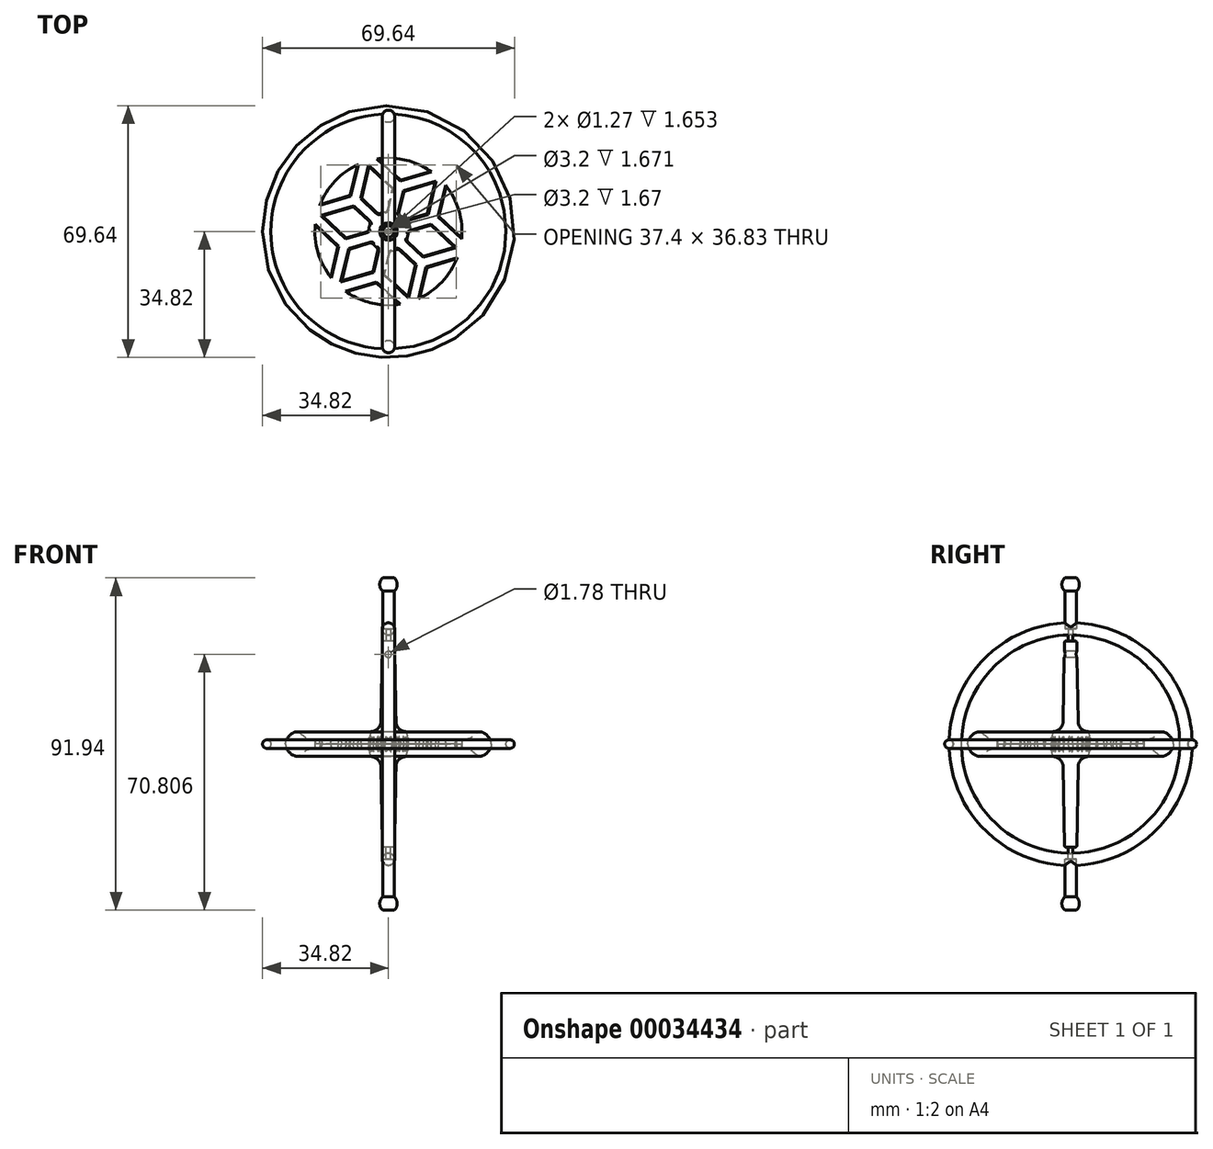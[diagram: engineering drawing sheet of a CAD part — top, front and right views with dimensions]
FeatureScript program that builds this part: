
annotation { "Feature Type Name" : "Feature", "Feature Type Description" : "" }
export const myFeature = defineFeature(function(context is Context, id is Id, definition is map)
    precondition{}
    {
        {
            var Q0;
            Q0=qCreatedBy(makeId("Top.planeOp"),FACE);
            var sketch = newSketch(context, id + "F0", { "sketchPlane" : qUnion([Q0])});
            skCircle(sketch, "E0", {"center": v(0, 0) * mm, "radius": 5.46 * mm});
            skSolve(sketch);
        }
        {
            var Q0;
            Q0 = qSketchRegion(id + "F0", true);
            extrude(context, id + "F1", {"entities" : qUnion([Q0]), "depth" : 3.43 * mm, "hasDraft" : true, "draftAngle" : 8 * degree, "draftPullDirection" : true});
        }
        {
            var Q0;
            Q0=qCreatedBy(makeId("Front.planeOp"),FACE);
            var sketch = newSketch(context, id + "F2", { "sketchPlane" : qUnion([Q0])});
            skLineSegment(sketch, "E1.0", {"start": v(-4.98, 3.43) * mm, "end": v(4.98, 3.43) * mm, "construction": true});
            skLineSegment(sketch, "E2", {"start": v(0, 3.43) * mm, "end": v(0, 14.25) * mm, "construction": true});
            skPoint(sketch, "E2.endSnap0", {"position": v(0, 3.43) * mm});
            skArc(sketch, "E3", {"start": v(2.07, 6.34) * mm, "mid": v(2.92, 4.28) * mm, "end": v(4.98, 3.43) * mm});
            skLineSegment(sketch, "E4", {"start": v(2.07, 6.34) * mm, "end": v(2.07, 12.69) * mm, "construction": true});
            skLineSegment(sketch, "E5", {"start": v(2.07, 6.34) * mm, "end": v(0, 6.34) * mm});
            skLineSegment(sketch, "E6", {"start": v(0, 6.34) * mm, "end": v(0, 3.43) * mm});
            skLineSegment(sketch, "E7", {"start": v(0, 3.43) * mm, "end": v(4.98, 3.43) * mm});
            skSolve(sketch);
        }
        {
            var Q0;
            Q0=makeQuery(id+"F2.imprint","IMPRINT",FACE,{"disambiguationData":[TD([[makeQuery(id+"F2.imprint","IMPRINT",EDGE,{"derivedFrom":sQuery(id+"F2.wireOp",EDGE,"E3")}),-1.0]])]});
            var Q1;
            Q1=sQuery(id+"F2.wireOp",EDGE,"E2");
            revolve(context, id + "F3", {"operationType" : NewBodyOperationType.ADD, "entities" : qUnion([Q0]), "axis" : qUnion([Q1]), "revolveType" : RevolveType.FULL});
        }
        {
            var Q0;
            Q0=makeQuery(id+"F3.opRevolve","SWEPT_FACE",FACE,{"disambiguationData":[OSD([sQuery(id+"F2.wireOp",EDGE,"E5")])]});
            var sketch = newSketch(context, id + "F4", { "sketchPlane" : qUnion([Q0])});
            skCircle(sketch, "E8.1", {"center": v(0, 0) * mm, "radius": 2.07 * mm});
            skSolve(sketch);
        }
        {
            var Q0;
            Q0 = qSketchRegion(id + "F4", true);
            extrude(context, id + "F5", {"entities" : qUnion([Q0]), "operationType" : NewBodyOperationType.ADD, "depth" : 22.17 * mm, "hasDraft" : true, "draftAngle" : 1 * degree, "draftPullDirection" : true});
        }
        {
            var Q0;
            Q0=qCreatedBy(makeId("Top.planeOp"),FACE);
            var sketch = newSketch(context, id + "F6", { "sketchPlane" : qUnion([Q0])});
            skLineSegment(sketch, "E9", {"start": v(0, 0) * mm, "end": v(-9.24, 8.72) * mm});
            skLineSegment(sketch, "E10", {"start": v(0, 0) * mm, "end": v(-12.17, -3.64) * mm});
            skLineSegment(sketch, "E11", {"start": v(-9.24, 8.72) * mm, "end": v(-21.4, 5.08) * mm});
            skLineSegment(sketch, "E12", {"start": v(-21.4, 5.08) * mm, "end": v(-12.17, -3.64) * mm});
            skLineSegment(sketch, "E13", {"start": v(-21.4, 5.08) * mm, "end": v(0, 0) * mm, "construction": true});
            skLineSegment(sketch, "E14", {"start": v(-12.17, -3.64) * mm, "end": v(-15.1, -16) * mm});
            skLineSegment(sketch, "E15.0", {"start": v(-3.14, 0.74) * mm, "end": v(-11.74, -1.83) * mm});
            skLineSegment(sketch, "E15.1", {"start": v(-3.14, 0.74) * mm, "end": v(-9.67, 6.9) * mm});
            skLineSegment(sketch, "E15.2", {"start": v(-9.67, 6.9) * mm, "end": v(-18.26, 4.33) * mm});
            skLineSegment(sketch, "E15.3", {"start": v(-18.26, 4.33) * mm, "end": v(-11.74, -1.83) * mm});
            skLineSegment(sketch, "E16.0", {"start": v(3.14, -0.74) * mm, "end": v(-12.6, -5.45) * mm});
            skLineSegment(sketch, "E16.1", {"start": v(3.14, -0.74) * mm, "end": v(-8.8, 10.53) * mm});
            skLineSegment(sketch, "E16.2", {"start": v(-8.8, 10.53) * mm, "end": v(-24.54, 5.82) * mm});
            skLineSegment(sketch, "E16.3", {"start": v(-24.54, 5.82) * mm, "end": v(-12.6, -5.45) * mm});
            skLineSegment(sketch, "E17.0", {"start": v(-13.74, -3.27) * mm, "end": v(-16.67, -15.62) * mm});
            skLineSegment(sketch, "E18.0", {"start": v(-10.6, -4.01) * mm, "end": v(-13.53, -16.37) * mm});
            skLineSegment(sketch, "E19", {"start": v(-13.53, -16.37) * mm, "end": v(-15.1, -16) * mm});
            skLineSegment(sketch, "E20", {"start": v(-16.67, -15.62) * mm, "end": v(-15.1, -16) * mm});
            skSolve(sketch);
        }
        {
            var Q0;
            Q0=makeQuery(id+"F6.imprint","IMPRINT",FACE,{"disambiguationData":[TD([[makeQuery(id+"F6.imprint","IMPRINT",EDGE,{"derivedFrom":sQuery(id+"F6.wireOp",EDGE,"E9")}),1.0]])]});
            var Q1;
            Q1=makeQuery(id+"F6.imprint","IMPRINT",FACE,{"disambiguationData":[TD([[makeQuery(id+"F6.imprint","IMPRINT",EDGE,{"derivedFrom":sQuery(id+"F6.wireOp",EDGE,"E9")}),-1.0]])]});
            var Q2;
            {var subQ0=sQuery(id+"F6.wireOp",EDGE,"E19");Q2=makeQuery(id+"F6.imprint","IMPRINT",FACE,{"disambiguationData":[TD([[makeQuery(id+"F6.imprint","IMPRINT",EDGE,{"derivedFrom":subQ0}),-1.0]])]});}
            var Q3;
            {var subQ0=sQuery(id+"F6.wireOp",EDGE,"E20");Q3=makeQuery(id+"F6.imprint","IMPRINT",FACE,{"disambiguationData":[TD([[makeQuery(id+"F6.imprint","IMPRINT",EDGE,{"derivedFrom":subQ0}),1.0]])]});}
            extrude(context, id + "F7", {"entities" : qUnion([Q0, Q1, Q2, Q3]), "depth" : 1.27 * mm, "hasDraft" : true, "draftAngle" : 10 * degree, "draftPullDirection" : true});
        }
        {
            var Q0;
            Q0=makeQuery(id+"F7.opExtrude","SWEPT_BODY",BODY,{"disambiguationData":[OSD([sQuery(id+"F6.wireOp",EDGE,"E15.0"),sQuery(id+"F6.wireOp",EDGE,"E15.1"),sQuery(id+"F6.wireOp",EDGE,"E15.2"),sQuery(id+"F6.wireOp",EDGE,"E15.3"),sQuery(id+"F6.wireOp",EDGE,"E16.0"),sQuery(id+"F6.wireOp",EDGE,"E16.1"),sQuery(id+"F6.wireOp",EDGE,"E16.2"),sQuery(id+"F6.wireOp",EDGE,"E16.3"),sQuery(id+"F6.wireOp",EDGE,"E17.0"),sQuery(id+"F6.wireOp",EDGE,"E18.0"),sQuery(id+"F6.wireOp",EDGE,"E19"),sQuery(id+"F6.wireOp",EDGE,"E20")])]});
            var Q1;
            Q1=sQuery(id+"F2.wireOp",EDGE,"E2");
            circularPattern(context, id + "F8", {"operationType" : NewBodyOperationType.ADD, "entities" : qUnion([Q0]), "axis" : qUnion([Q1]), "angle" : 60 * degree, "instanceCount" : 6});
        }
        {
            var Q0;
            Q0=qCreatedBy(makeId("Top.planeOp"),FACE);
            var sketch = newSketch(context, id + "F9", { "sketchPlane" : qUnion([Q0])});
            skCircle(sketch, "E21", {"center": v(0, 0) * mm, "radius": 20.32 * mm});
            skCircle(sketch, "E22", {"center": v(0, 0) * mm, "radius": 25.4 * mm});
            skSolve(sketch);
        }
        {
            var Q0;
            Q0=makeQuery(id+"F9.imprint","IMPRINT",FACE,{"disambiguationData":[TD([[makeQuery(id+"F9.imprint","IMPRINT",EDGE,{"derivedFrom":sQuery(id+"F9.wireOp",EDGE,"E21")}),-1.0]])]});
            extrude(context, id + "F10", {"entities" : qUnion([Q0]), "operationType" : NewBodyOperationType.ADD, "depth" : 1.27 * mm});
        }
        {
            var Q0;
            Q0=qCreatedBy(makeId("Front.planeOp"),FACE);
            var sketch = newSketch(context, id + "F11", { "sketchPlane" : qUnion([Q0])});
            skLineSegment(sketch, "E23.0", {"start": v(-25.4, 0) * mm, "end": v(25.4, 0) * mm, "construction": true});
            skLineSegment(sketch, "E24", {"start": v(25.4, 0) * mm, "end": v(28.45, 0) * mm, "construction": true});
            skLineSegment(sketch, "E25.0", {"start": v(-25.4, 1.27) * mm, "end": v(25.4, 1.27) * mm, "construction": true});
            skLineSegment(sketch, "E26", {"start": v(28.45, 0) * mm, "end": v(28.45, 3.38) * mm, "construction": true});
            skLineSegment(sketch, "E27.0", {"start": v(15.77, 1.27) * mm, "end": v(20.32, 1.27) * mm, "construction": true});
            skLineSegment(sketch, "E28", {"start": v(20.32, 1.27) * mm, "end": v(20.32, 3.38) * mm, "construction": true});
            skLineSegment(sketch, "E29", {"start": v(25.32, 0) * mm, "end": v(25.32, 3.38) * mm, "construction": true});
            skLineSegment(sketch, "E30", {"start": v(28.45, 3.38) * mm, "end": v(20.32, 3.38) * mm, "construction": true});
            skFitSpline(sketch, "E31", {"points": [v(20.32, 1.27) * mm, v(25.32, 3.38) * mm, v(28.45, 0) * mm], "startDerivative": vector(18.65, 0) * mm, "endDerivative": vector(0, -10.57) * mm});
            skLineSegment(sketch, "E32", {"start": v(20.32, 1.27) * mm, "end": v(25.4, 1.27) * mm});
            skLineSegment(sketch, "E33", {"start": v(25.4, 1.27) * mm, "end": v(25.4, 0) * mm});
            skLineSegment(sketch, "E34", {"start": v(25.4, 0) * mm, "end": v(28.45, 0) * mm});
            skSolve(sketch);
        }
        {
            var Q0;
            Q0 = qSketchRegion(id + "F11", true);
            var Q1;
            Q1=sQuery(id+"F2.wireOp",EDGE,"E2");
            revolve(context, id + "F12", {"operationType" : NewBodyOperationType.ADD, "entities" : qUnion([Q0]), "axis" : qUnion([Q1]), "revolveType" : RevolveType.FULL});
        }
        {
            var Q0;
            Q0=makeQuery(id+"F5.opExtrude","CAP_EDGE",EDGE,{"disambiguationData":[OSD([sQuery(id+"F4.wireOp",EDGE,"E8.1")])],"isStart":false});
            fillet(context, id + "F13", {"entities" : qUnion([Q0]), "radius" : 0.38 * mm, "tangentPropagation" : true, "allowEdgeOverflow" : false});
        }
        {
            var Q0;
            Q0=makeQuery(id+"F5.opExtrude","CAP_FACE",FACE,{"disambiguationData":[OSD([sQuery(id+"F4.wireOp",EDGE,"E8.1")])],"isStart":false});
            var sketch = newSketch(context, id + "F14", { "sketchPlane" : qUnion([Q0])});
            skCircle(sketch, "E35", {"center": v(0, 0) * mm, "radius": 0.64 * mm});
            skSolve(sketch);
        }
        {
            var Q0;
            Q0 = qSketchRegion(id + "F14", true);
            extrude(context, id + "F15", {"entities" : qUnion([Q0]), "operationType" : NewBodyOperationType.ADD, "depth" : 3.3 * mm});
        }
        {
            var Q0;
            {var subQ0=makeQuery(id+"F7.opExtrude","CAP_FACE",FACE,{"disambiguationData":[OSD([sQuery(id+"F6.wireOp",EDGE,"E15.0"),sQuery(id+"F6.wireOp",EDGE,"E15.1"),sQuery(id+"F6.wireOp",EDGE,"E15.2"),sQuery(id+"F6.wireOp",EDGE,"E15.3"),sQuery(id+"F6.wireOp",EDGE,"E16.0"),sQuery(id+"F6.wireOp",EDGE,"E16.1"),sQuery(id+"F6.wireOp",EDGE,"E16.2"),sQuery(id+"F6.wireOp",EDGE,"E16.3"),sQuery(id+"F6.wireOp",EDGE,"E17.0"),sQuery(id+"F6.wireOp",EDGE,"E18.0"),sQuery(id+"F6.wireOp",EDGE,"E19"),sQuery(id+"F6.wireOp",EDGE,"E20")])],"isStart":false});Q0=makeQuery(id+"F8.boolean.opBoolean","INTERSECT",EDGE,{"disambiguationData":[OD(4.0)],"derivedFrom":[makeQuery(id+"F1.opExtrude","SWEPT_FACE",FACE,{"disambiguationData":[OSD([sQuery(id+"F0.wireOp",EDGE,"E0")])]}),subQ0,makeQuery(id+"F8.opPattern","COPY",FACE,{"derivedFrom":subQ0,"instanceName":"1"}),makeQuery(id+"F8.opPattern","COPY",FACE,{"derivedFrom":subQ0,"instanceName":"2"}),makeQuery(id+"F8.opPattern","COPY",FACE,{"derivedFrom":subQ0,"instanceName":"3"}),makeQuery(id+"F8.opPattern","COPY",FACE,{"derivedFrom":subQ0,"instanceName":"4"}),makeQuery(id+"F8.opPattern","COPY",FACE,{"derivedFrom":subQ0,"instanceName":"5"})]});}
            var Q1;
            {var subQ0=makeQuery(id+"F7.opExtrude","CAP_FACE",FACE,{"disambiguationData":[OSD([sQuery(id+"F6.wireOp",EDGE,"E15.0"),sQuery(id+"F6.wireOp",EDGE,"E15.1"),sQuery(id+"F6.wireOp",EDGE,"E15.2"),sQuery(id+"F6.wireOp",EDGE,"E15.3"),sQuery(id+"F6.wireOp",EDGE,"E16.0"),sQuery(id+"F6.wireOp",EDGE,"E16.1"),sQuery(id+"F6.wireOp",EDGE,"E16.2"),sQuery(id+"F6.wireOp",EDGE,"E16.3"),sQuery(id+"F6.wireOp",EDGE,"E17.0"),sQuery(id+"F6.wireOp",EDGE,"E18.0"),sQuery(id+"F6.wireOp",EDGE,"E19"),sQuery(id+"F6.wireOp",EDGE,"E20")])],"isStart":false});Q1=makeQuery(id+"F8.boolean.opBoolean","INTERSECT",EDGE,{"disambiguationData":[OD(5.0)],"derivedFrom":[makeQuery(id+"F1.opExtrude","SWEPT_FACE",FACE,{"disambiguationData":[OSD([sQuery(id+"F0.wireOp",EDGE,"E0")])]}),subQ0,makeQuery(id+"F8.opPattern","COPY",FACE,{"derivedFrom":subQ0,"instanceName":"1"}),makeQuery(id+"F8.opPattern","COPY",FACE,{"derivedFrom":subQ0,"instanceName":"2"}),makeQuery(id+"F8.opPattern","COPY",FACE,{"derivedFrom":subQ0,"instanceName":"3"}),makeQuery(id+"F8.opPattern","COPY",FACE,{"derivedFrom":subQ0,"instanceName":"4"}),makeQuery(id+"F8.opPattern","COPY",FACE,{"derivedFrom":subQ0,"instanceName":"5"})]});}
            var Q2;
            {var subQ0=makeQuery(id+"F7.opExtrude","CAP_FACE",FACE,{"disambiguationData":[OSD([sQuery(id+"F6.wireOp",EDGE,"E15.0"),sQuery(id+"F6.wireOp",EDGE,"E15.1"),sQuery(id+"F6.wireOp",EDGE,"E15.2"),sQuery(id+"F6.wireOp",EDGE,"E15.3"),sQuery(id+"F6.wireOp",EDGE,"E16.0"),sQuery(id+"F6.wireOp",EDGE,"E16.1"),sQuery(id+"F6.wireOp",EDGE,"E16.2"),sQuery(id+"F6.wireOp",EDGE,"E16.3"),sQuery(id+"F6.wireOp",EDGE,"E17.0"),sQuery(id+"F6.wireOp",EDGE,"E18.0"),sQuery(id+"F6.wireOp",EDGE,"E19"),sQuery(id+"F6.wireOp",EDGE,"E20")])],"isStart":false});Q2=makeQuery(id+"F8.boolean.opBoolean","INTERSECT",EDGE,{"disambiguationData":[OD(1.0)],"derivedFrom":[makeQuery(id+"F1.opExtrude","SWEPT_FACE",FACE,{"disambiguationData":[OSD([sQuery(id+"F0.wireOp",EDGE,"E0")])]}),subQ0,makeQuery(id+"F8.opPattern","COPY",FACE,{"derivedFrom":subQ0,"instanceName":"1"}),makeQuery(id+"F8.opPattern","COPY",FACE,{"derivedFrom":subQ0,"instanceName":"2"}),makeQuery(id+"F8.opPattern","COPY",FACE,{"derivedFrom":subQ0,"instanceName":"3"}),makeQuery(id+"F8.opPattern","COPY",FACE,{"derivedFrom":subQ0,"instanceName":"4"}),makeQuery(id+"F8.opPattern","COPY",FACE,{"derivedFrom":subQ0,"instanceName":"5"})]});}
            var Q3;
            {var subQ0=makeQuery(id+"F7.opExtrude","CAP_FACE",FACE,{"disambiguationData":[OSD([sQuery(id+"F6.wireOp",EDGE,"E15.0"),sQuery(id+"F6.wireOp",EDGE,"E15.1"),sQuery(id+"F6.wireOp",EDGE,"E15.2"),sQuery(id+"F6.wireOp",EDGE,"E15.3"),sQuery(id+"F6.wireOp",EDGE,"E16.0"),sQuery(id+"F6.wireOp",EDGE,"E16.1"),sQuery(id+"F6.wireOp",EDGE,"E16.2"),sQuery(id+"F6.wireOp",EDGE,"E16.3"),sQuery(id+"F6.wireOp",EDGE,"E17.0"),sQuery(id+"F6.wireOp",EDGE,"E18.0"),sQuery(id+"F6.wireOp",EDGE,"E19"),sQuery(id+"F6.wireOp",EDGE,"E20")])],"isStart":false});Q3=makeQuery(id+"F8.boolean.opBoolean","INTERSECT",EDGE,{"disambiguationData":[OD(0.0)],"derivedFrom":[makeQuery(id+"F1.opExtrude","SWEPT_FACE",FACE,{"disambiguationData":[OSD([sQuery(id+"F0.wireOp",EDGE,"E0")])]}),subQ0,makeQuery(id+"F8.opPattern","COPY",FACE,{"derivedFrom":subQ0,"instanceName":"1"}),makeQuery(id+"F8.opPattern","COPY",FACE,{"derivedFrom":subQ0,"instanceName":"2"}),makeQuery(id+"F8.opPattern","COPY",FACE,{"derivedFrom":subQ0,"instanceName":"3"}),makeQuery(id+"F8.opPattern","COPY",FACE,{"derivedFrom":subQ0,"instanceName":"4"}),makeQuery(id+"F8.opPattern","COPY",FACE,{"derivedFrom":subQ0,"instanceName":"5"})]});}
            var Q4;
            {var subQ0=makeQuery(id+"F7.opExtrude","CAP_FACE",FACE,{"disambiguationData":[OSD([sQuery(id+"F6.wireOp",EDGE,"E15.0"),sQuery(id+"F6.wireOp",EDGE,"E15.1"),sQuery(id+"F6.wireOp",EDGE,"E15.2"),sQuery(id+"F6.wireOp",EDGE,"E15.3"),sQuery(id+"F6.wireOp",EDGE,"E16.0"),sQuery(id+"F6.wireOp",EDGE,"E16.1"),sQuery(id+"F6.wireOp",EDGE,"E16.2"),sQuery(id+"F6.wireOp",EDGE,"E16.3"),sQuery(id+"F6.wireOp",EDGE,"E17.0"),sQuery(id+"F6.wireOp",EDGE,"E18.0"),sQuery(id+"F6.wireOp",EDGE,"E19"),sQuery(id+"F6.wireOp",EDGE,"E20")])],"isStart":false});Q4=makeQuery(id+"F8.boolean.opBoolean","INTERSECT",EDGE,{"disambiguationData":[OD(2.0)],"derivedFrom":[makeQuery(id+"F1.opExtrude","SWEPT_FACE",FACE,{"disambiguationData":[OSD([sQuery(id+"F0.wireOp",EDGE,"E0")])]}),subQ0,makeQuery(id+"F8.opPattern","COPY",FACE,{"derivedFrom":subQ0,"instanceName":"1"}),makeQuery(id+"F8.opPattern","COPY",FACE,{"derivedFrom":subQ0,"instanceName":"2"}),makeQuery(id+"F8.opPattern","COPY",FACE,{"derivedFrom":subQ0,"instanceName":"3"}),makeQuery(id+"F8.opPattern","COPY",FACE,{"derivedFrom":subQ0,"instanceName":"4"}),makeQuery(id+"F8.opPattern","COPY",FACE,{"derivedFrom":subQ0,"instanceName":"5"})]});}
            var Q5;
            {var subQ0=makeQuery(id+"F7.opExtrude","CAP_FACE",FACE,{"disambiguationData":[OSD([sQuery(id+"F6.wireOp",EDGE,"E15.0"),sQuery(id+"F6.wireOp",EDGE,"E15.1"),sQuery(id+"F6.wireOp",EDGE,"E15.2"),sQuery(id+"F6.wireOp",EDGE,"E15.3"),sQuery(id+"F6.wireOp",EDGE,"E16.0"),sQuery(id+"F6.wireOp",EDGE,"E16.1"),sQuery(id+"F6.wireOp",EDGE,"E16.2"),sQuery(id+"F6.wireOp",EDGE,"E16.3"),sQuery(id+"F6.wireOp",EDGE,"E17.0"),sQuery(id+"F6.wireOp",EDGE,"E18.0"),sQuery(id+"F6.wireOp",EDGE,"E19"),sQuery(id+"F6.wireOp",EDGE,"E20")])],"isStart":false});Q5=makeQuery(id+"F8.boolean.opBoolean","INTERSECT",EDGE,{"disambiguationData":[OD(3.0)],"derivedFrom":[makeQuery(id+"F1.opExtrude","SWEPT_FACE",FACE,{"disambiguationData":[OSD([sQuery(id+"F0.wireOp",EDGE,"E0")])]}),subQ0,makeQuery(id+"F8.opPattern","COPY",FACE,{"derivedFrom":subQ0,"instanceName":"1"}),makeQuery(id+"F8.opPattern","COPY",FACE,{"derivedFrom":subQ0,"instanceName":"2"}),makeQuery(id+"F8.opPattern","COPY",FACE,{"derivedFrom":subQ0,"instanceName":"3"}),makeQuery(id+"F8.opPattern","COPY",FACE,{"derivedFrom":subQ0,"instanceName":"4"}),makeQuery(id+"F8.opPattern","COPY",FACE,{"derivedFrom":subQ0,"instanceName":"5"})]});}
            var Q6;
            Q6=makeQuery(id+"F8.boolean.opBoolean","INTERSECT",EDGE,{"derivedFrom":[makeQuery(id+"F1.opExtrude","SWEPT_FACE",FACE,{"disambiguationData":[OSD([sQuery(id+"F0.wireOp",EDGE,"E0")])]}),makeQuery(id+"F8.opPattern","COPY",FACE,{"derivedFrom":makeQuery(id+"F7.opExtrude","SWEPT_FACE",FACE,{"disambiguationData":[OSD([sQuery(id+"F6.wireOp",EDGE,"E16.0")])]}),"instanceName":"2"})]});
            var Q7;
            Q7=makeQuery(id+"F8.boolean.opBoolean","INTERSECT",EDGE,{"derivedFrom":[makeQuery(id+"F1.opExtrude","SWEPT_FACE",FACE,{"disambiguationData":[OSD([sQuery(id+"F0.wireOp",EDGE,"E0")])]}),makeQuery(id+"F8.opPattern","COPY",FACE,{"derivedFrom":makeQuery(id+"F7.opExtrude","SWEPT_FACE",FACE,{"disambiguationData":[OSD([sQuery(id+"F6.wireOp",EDGE,"E15.0")])]}),"instanceName":"2"})]});
            var Q8;
            Q8=makeQuery(id+"F8.boolean.opBoolean","INTERSECT",EDGE,{"derivedFrom":[makeQuery(id+"F1.opExtrude","SWEPT_FACE",FACE,{"disambiguationData":[OSD([sQuery(id+"F0.wireOp",EDGE,"E0")])]}),makeQuery(id+"F8.opPattern","COPY",FACE,{"derivedFrom":makeQuery(id+"F7.opExtrude","SWEPT_FACE",FACE,{"disambiguationData":[OSD([sQuery(id+"F6.wireOp",EDGE,"E16.0")])]}),"instanceName":"1"})]});
            var Q9;
            Q9=makeQuery(id+"F8.boolean.opBoolean","INTERSECT",EDGE,{"derivedFrom":[makeQuery(id+"F1.opExtrude","SWEPT_FACE",FACE,{"disambiguationData":[OSD([sQuery(id+"F0.wireOp",EDGE,"E0")])]}),makeQuery(id+"F8.opPattern","COPY",FACE,{"derivedFrom":makeQuery(id+"F7.opExtrude","SWEPT_FACE",FACE,{"disambiguationData":[OSD([sQuery(id+"F6.wireOp",EDGE,"E15.0")])]}),"instanceName":"1"})]});
            var Q10;
            Q10=makeQuery(id+"F8.boolean.opBoolean","INTERSECT",EDGE,{"derivedFrom":[makeQuery(id+"F1.opExtrude","SWEPT_FACE",FACE,{"disambiguationData":[OSD([sQuery(id+"F0.wireOp",EDGE,"E0")])]}),makeQuery(id+"F7.opExtrude","SWEPT_FACE",FACE,{"disambiguationData":[OSD([sQuery(id+"F6.wireOp",EDGE,"E16.0")])]})]});
            var Q11;
            Q11=makeQuery(id+"F8.boolean.opBoolean","INTERSECT",EDGE,{"derivedFrom":[makeQuery(id+"F1.opExtrude","SWEPT_FACE",FACE,{"disambiguationData":[OSD([sQuery(id+"F0.wireOp",EDGE,"E0")])]}),makeQuery(id+"F7.opExtrude","SWEPT_FACE",FACE,{"disambiguationData":[OSD([sQuery(id+"F6.wireOp",EDGE,"E15.0")])]})]});
            var Q12;
            Q12=makeQuery(id+"F8.boolean.opBoolean","INTERSECT",EDGE,{"derivedFrom":[makeQuery(id+"F1.opExtrude","SWEPT_FACE",FACE,{"disambiguationData":[OSD([sQuery(id+"F0.wireOp",EDGE,"E0")])]}),makeQuery(id+"F7.opExtrude","SWEPT_FACE",FACE,{"disambiguationData":[OSD([sQuery(id+"F6.wireOp",EDGE,"E15.1")])]})]});
            var Q13;
            Q13=makeQuery(id+"F8.boolean.opBoolean","INTERSECT",EDGE,{"derivedFrom":[makeQuery(id+"F1.opExtrude","SWEPT_FACE",FACE,{"disambiguationData":[OSD([sQuery(id+"F0.wireOp",EDGE,"E0")])]}),makeQuery(id+"F7.opExtrude","SWEPT_FACE",FACE,{"disambiguationData":[OSD([sQuery(id+"F6.wireOp",EDGE,"E16.1")])]})]});
            var Q14;
            Q14=makeQuery(id+"F8.boolean.opBoolean","INTERSECT",EDGE,{"derivedFrom":[makeQuery(id+"F1.opExtrude","SWEPT_FACE",FACE,{"disambiguationData":[OSD([sQuery(id+"F0.wireOp",EDGE,"E0")])]}),makeQuery(id+"F8.opPattern","COPY",FACE,{"derivedFrom":makeQuery(id+"F7.opExtrude","SWEPT_FACE",FACE,{"disambiguationData":[OSD([sQuery(id+"F6.wireOp",EDGE,"E16.0")])]}),"instanceName":"4"})]});
            var Q15;
            Q15=makeQuery(id+"F8.boolean.opBoolean","INTERSECT",EDGE,{"derivedFrom":[makeQuery(id+"F1.opExtrude","SWEPT_FACE",FACE,{"disambiguationData":[OSD([sQuery(id+"F0.wireOp",EDGE,"E0")])]}),makeQuery(id+"F8.opPattern","COPY",FACE,{"derivedFrom":makeQuery(id+"F7.opExtrude","SWEPT_FACE",FACE,{"disambiguationData":[OSD([sQuery(id+"F6.wireOp",EDGE,"E15.0")])]}),"instanceName":"4"})]});
            var Q16;
            Q16=makeQuery(id+"F8.boolean.opBoolean","INTERSECT",EDGE,{"derivedFrom":[makeQuery(id+"F1.opExtrude","SWEPT_FACE",FACE,{"disambiguationData":[OSD([sQuery(id+"F0.wireOp",EDGE,"E0")])]}),makeQuery(id+"F8.opPattern","COPY",FACE,{"derivedFrom":makeQuery(id+"F7.opExtrude","SWEPT_FACE",FACE,{"disambiguationData":[OSD([sQuery(id+"F6.wireOp",EDGE,"E16.0")])]}),"instanceName":"3"})]});
            var Q17;
            Q17=makeQuery(id+"F8.boolean.opBoolean","INTERSECT",EDGE,{"derivedFrom":[makeQuery(id+"F1.opExtrude","SWEPT_FACE",FACE,{"disambiguationData":[OSD([sQuery(id+"F0.wireOp",EDGE,"E0")])]}),makeQuery(id+"F8.opPattern","COPY",FACE,{"derivedFrom":makeQuery(id+"F7.opExtrude","SWEPT_FACE",FACE,{"disambiguationData":[OSD([sQuery(id+"F6.wireOp",EDGE,"E15.0")])]}),"instanceName":"3"})]});
            fillet(context, id + "F16", {"entities" : qUnion([Q0, Q1, Q2, Q3, Q4, Q5, Q6, Q7, Q8, Q9, Q10, Q11, Q12, Q13, Q14, Q15, Q16, Q17]), "radius" : 1.02 * mm, "tangentPropagation" : true, "allowEdgeOverflow" : false});
        }
        {
            var Q0;
            Q0=makeQuery(id+"F3.opRevolve","SWEPT_FACE",FACE,{"disambiguationData":[OSD([sQuery(id+"F2.wireOp",EDGE,"E3")])]});
            fillet(context, id + "F17", {"entities" : qUnion([Q0]), "radius" : 0.25 * mm, "tangentPropagation" : true, "allowEdgeOverflow" : false});
        }
        {
            var Q0;
            Q0=makeQuery(id+"F1.opExtrude","SWEPT_BODY",BODY,{"disambiguationData":[OSD([sQuery(id+"F0.wireOp",EDGE,"E0")])]});
            var Q1;
            Q1=qCreatedBy(makeId("Top.planeOp"),FACE);
            mirror(context, id + "F18", {"operationType" : NewBodyOperationType.ADD, "entities" : qUnion([Q0]), "mirrorPlane" : qUnion([Q1])});
        }
        {
            var Q0;
            Q0=qCreatedBy(makeId("Front.planeOp"),FACE);
            var sketch = newSketch(context, id + "F19", { "sketchPlane" : qUnion([Q0])});
            skLineSegment(sketch, "E36", {"start": v(0, 0) * mm, "end": v(0, 24.84) * mm, "construction": true});
            skCircle(sketch, "E37", {"center": v(0, 24.84) * mm, "radius": 0.89 * mm});
            skSolve(sketch);
        }
        {
            var Q0;
            Q0 = qSketchRegion(id + "F19", true);
            var Q1;
            Q1=sQuery(id+"F19.wireOp",EDGE,"E37");
            extrude(context, id + "F20", {"entities" : qUnion([Q0]), "operationType" : NewBodyOperationType.REMOVE, "surfaceEntities" : qUnion([Q1]), "endBound" : BoundingType.THROUGH_ALL, "oppositeDirection" : true, "depth" : 25.4 * mm, "hasSecondDirection" : true, "secondDirectionBound" : SecondDirectionBoundingType.THROUGH_ALL, "secondDirectionOppositeDirection" : false, "secondDirectionDepth" : 25.4 * mm});
        }
        {
            var Q0;
            Q0=qCreatedBy(makeId("Right.planeOp"),FACE);
            var sketch = newSketch(context, id + "F21", { "sketchPlane" : qUnion([Q0])});
            skCircle(sketch, "E38", {"center": v(0, 0) * mm, "radius": 31.88 * mm});
            skSolve(sketch);
        }
        {
            var Q0;
            Q0=qCreatedBy(makeId("Top.planeOp"),FACE);
            var sketch = newSketch(context, id + "F22", { "sketchPlane" : qUnion([Q0])});
            skLineSegment(sketch, "E39.0", {"start": v(0, 31.88) * mm, "end": v(0, -31.88) * mm, "construction": true});
            skCircle(sketch, "E40", {"center": v(0, -31.88) * mm, "radius": 1.7 * mm});
            skSolve(sketch);
        }
        {
            var Q0;
            Q0=makeQuery(id+"F22.imprint","IMPRINT",FACE,{"disambiguationData":[TD([[makeQuery(id+"F22.imprint","IMPRINT",EDGE,{"derivedFrom":sQuery(id+"F22.wireOp",EDGE,"E40")}),1.0]])]});
            var Q1;
            Q1=sQuery(id+"F21.wireOp",EDGE,"E38");
            sweep(context, id + "F23", {"profiles" : qUnion([Q0]), "path" : qUnion([Q1])});
        }
        {
            var Q0;
            Q0=makeQuery(id+"F1.opExtrude","SWEPT_BODY",BODY,{"disambiguationData":[OSD([sQuery(id+"F0.wireOp",EDGE,"E0")])]});
            var Q1;
            Q1=makeQuery(id+"F23.opSweep","SWEPT_BODY",BODY,{"disambiguationData":[OSD([sQuery(id+"F21.wireOp",EDGE,"E38"),sQuery(id+"F22.wireOp",EDGE,"E40")])]});
            booleanBodies(context, id + "F24", {"operationType" : BooleanOperationType.SUBTRACTION, "tools" : qUnion([Q0]), "targets" : qUnion([Q1]), "keepTools" : true});
        }
        {
            var Q0;
            Q0=qCreatedBy(makeId("Top.planeOp"),FACE);
            var sketch = newSketch(context, id + "F25", { "sketchPlane" : qUnion([Q0])});
            skCircle(sketch, "E41", {"center": v(0, 0) * mm, "radius": 33.66 * mm});
            skSolve(sketch);
        }
        {
            var Q0;
            Q0=qCreatedBy(makeId("Front.planeOp"),FACE);
            var sketch = newSketch(context, id + "F26", { "sketchPlane" : qUnion([Q0])});
            skLineSegment(sketch, "E42.0", {"start": v(-33.66, 0) * mm, "end": v(33.66, 0) * mm, "construction": true});
            skCircle(sketch, "E43", {"center": v(-33.66, 0) * mm, "radius": 1.16 * mm});
            skSolve(sketch);
        }
        {
            var Q0;
            Q0=makeQuery(id+"F26.imprint","IMPRINT",FACE,{"disambiguationData":[TD([[makeQuery(id+"F26.imprint","IMPRINT",EDGE,{"derivedFrom":sQuery(id+"F26.wireOp",EDGE,"E43")}),1.0]])]});
            var Q1;
            Q1=sQuery(id+"F25.wireOp",EDGE,"E41");
            sweep(context, id + "F27", {"operationType" : NewBodyOperationType.ADD, "profiles" : qUnion([Q0]), "path" : qUnion([Q1])});
        }
        {
            var Q0;
            Q0=qCreatedBy(makeId("Front.planeOp"),FACE);
            var sketch = newSketch(context, id + "F28", { "sketchPlane" : qUnion([Q0])});
            skLineSegment(sketch, "E44", {"start": v(0, 0) * mm, "end": v(0, 31.88) * mm});
            skLineSegment(sketch, "E45.0", {"start": v(0, 31.88) * mm, "end": v(0, -31.88) * mm, "construction": true});
            skLineSegment(sketch, "E46.bottom", {"start": v(0, 31.88) * mm, "end": v(-1.6, 31.88) * mm});
            skLineSegment(sketch, "E46.top", {"start": v(0, 42.3) * mm, "end": v(-1.6, 42.3) * mm, "construction": true});
            skLineSegment(sketch, "E46.left", {"start": v(0, 31.88) * mm, "end": v(0, 42.3) * mm});
            skLineSegment(sketch, "E46.right", {"start": v(-1.6, 31.88) * mm, "end": v(-1.6, 42.3) * mm});
            skArc(sketch, "E47", {"start": v(-1.6, 45.97) * mm, "mid": v(-2.41, 44.13) * mm, "end": v(-1.6, 42.3) * mm});
            skLineSegment(sketch, "E48", {"start": v(-1.6, 42.3) * mm, "end": v(-1.6, 45.97) * mm, "construction": true});
            skLineSegment(sketch, "E49", {"start": v(-1.6, 45.97) * mm, "end": v(0, 45.97) * mm});
            skLineSegment(sketch, "E50", {"start": v(0, 45.97) * mm, "end": v(0, 42.3) * mm});
            skLineSegment(sketch, "E51", {"start": v(-2.41, 44.13) * mm, "end": v(0, 44.13) * mm, "construction": true});
            skSolve(sketch);
        }
        {
            var Q0;
            Q0 = qSketchRegion(id + "F28", true);
            var Q1;
            Q1=sQuery(id+"F28.wireOp",EDGE,"E44");
            revolve(context, id + "F29", {"entities" : qUnion([Q0]), "axis" : qUnion([Q1]), "revolveType" : RevolveType.FULL});
        }
        {
            var Q0;
            Q0=makeQuery(id+"F29.opRevolve","SWEPT_BODY",BODY,{"disambiguationData":[OSD([sQuery(id+"F28.wireOp",EDGE,"E46.bottom"),sQuery(id+"F28.wireOp",EDGE,"E46.left"),sQuery(id+"F28.wireOp",EDGE,"E46.right"),sQuery(id+"F28.wireOp",EDGE,"E47"),sQuery(id+"F28.wireOp",EDGE,"E49"),sQuery(id+"F28.wireOp",EDGE,"E50")])]});
            var Q1;
            Q1=qCreatedBy(makeId("Top.planeOp"),FACE);
            mirror(context, id + "F30", {"entities" : qUnion([Q0]), "mirrorPlane" : qUnion([Q1])});
        }
        {
            var Q0;
            Q0=makeQuery(id+"F29.opRevolve","SWEPT_BODY",BODY,{"disambiguationData":[OSD([sQuery(id+"F28.wireOp",EDGE,"E46.bottom"),sQuery(id+"F28.wireOp",EDGE,"E46.left"),sQuery(id+"F28.wireOp",EDGE,"E46.right"),sQuery(id+"F28.wireOp",EDGE,"E47"),sQuery(id+"F28.wireOp",EDGE,"E49"),sQuery(id+"F28.wireOp",EDGE,"E50")])]});
            var Q1;
            Q1=makeQuery(id+"F30.opPattern","COPY",BODY,{"derivedFrom":makeQuery(id+"F29.opRevolve","SWEPT_BODY",BODY,{"disambiguationData":[OSD([sQuery(id+"F28.wireOp",EDGE,"E46.bottom"),sQuery(id+"F28.wireOp",EDGE,"E46.left"),sQuery(id+"F28.wireOp",EDGE,"E46.right"),sQuery(id+"F28.wireOp",EDGE,"E47"),sQuery(id+"F28.wireOp",EDGE,"E49"),sQuery(id+"F28.wireOp",EDGE,"E50")])]}),"instanceName":"1"});
            var Q2;
            Q2=makeQuery(id+"F23.opSweep","SWEPT_BODY",BODY,{"disambiguationData":[OSD([sQuery(id+"F21.wireOp",EDGE,"E38"),sQuery(id+"F22.wireOp",EDGE,"E40")])]});
            booleanBodies(context, id + "F31", {"operationType" : BooleanOperationType.SUBTRACTION, "tools" : qUnion([Q0, Q1]), "targets" : qUnion([Q2]), "keepTools" : true});
        }
    });
